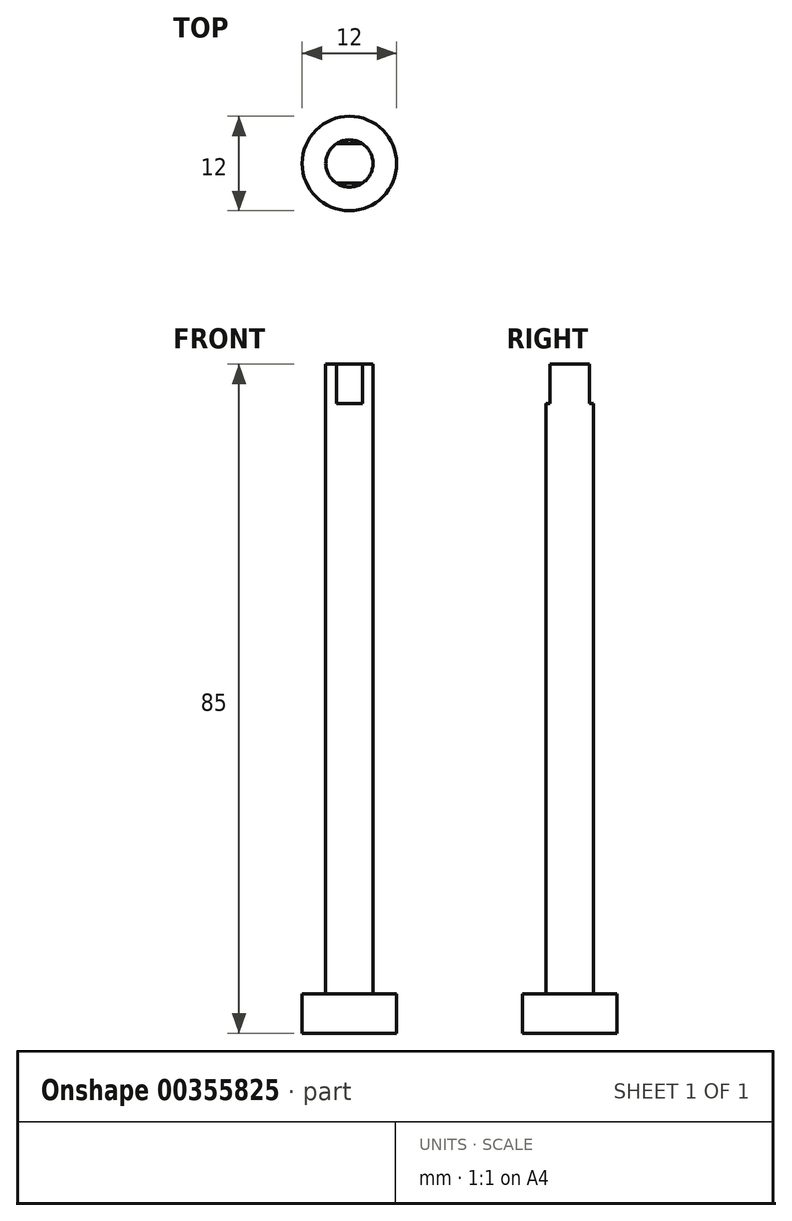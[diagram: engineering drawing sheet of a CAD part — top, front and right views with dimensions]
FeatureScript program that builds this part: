
annotation { "Feature Type Name" : "Feature", "Feature Type Description" : "" }
export const myFeature = defineFeature(function(context is Context, id is Id, definition is map)
    precondition{}
    {
        {
            var Q0;
            Q0=qCreatedBy(makeId("Top.planeOp"),FACE);
            var sketch = newSketch(context, id + "F0", { "sketchPlane" : qUnion([Q0])});
            skCircle(sketch, "E0", {"center": v(0, 0) * mm, "radius": 3 * mm});
            skSolve(sketch);
        }
        {
            var Q0;
            Q0 = qSketchRegion(id + "F0", true);
            extrude(context, id + "F1", {"entities" : qUnion([Q0]), "endBound" : BoundingType.SYMMETRIC, "depth" : 80 * mm});
        }
        {
            var Q0;
            Q0=makeQuery(id+"F1.opExtrude","CAP_FACE",FACE,{"disambiguationData":[OSD([sQuery(id+"F0.wireOp",EDGE,"E0")])],"isStart":true});
            var sketch = newSketch(context, id + "F2", { "sketchPlane" : qUnion([Q0])});
            skCircle(sketch, "E1", {"center": v(0, 0) * mm, "radius": 6 * mm});
            skSolve(sketch);
        }
        {
            var Q0;
            Q0=makeQuery(id+"F2.imprint","IMPRINT",FACE,{"disambiguationData":[TD([[makeQuery(id+"F2.imprint","IMPRINT",EDGE,{"derivedFrom":sQuery(id+"F2.wireOp",EDGE,"E1")}),1.0]])]});
            var Q1;
            Q1=makeQuery(id+"F2.imprint","IMPRINT",FACE,{"disambiguationData":[TD([[makeQuery(id+"F2.imprint","IMPRINT",EDGE,{"derivedFrom":makeQuery(id+"F1.opExtrude","CAP_EDGE",EDGE,{"disambiguationData":[OSD([sQuery(id+"F0.wireOp",EDGE,"E0")])],"isStart":true})}),-1.0]])]});
            extrude(context, id + "F3", {"entities" : qUnion([Q0, Q1]), "operationType" : NewBodyOperationType.ADD, "depth" : 5 * mm});
        }
        {
            var Q0;
            Q0=makeQuery(id+"F1.opExtrude","CAP_FACE",FACE,{"disambiguationData":[OSD([sQuery(id+"F0.wireOp",EDGE,"E0")])],"isStart":false});
            var sketch = newSketch(context, id + "F4", { "sketchPlane" : qUnion([Q0])});
            skLineSegment(sketch, "E2.bottom", {"start": v(4.53, -2.5) * mm, "end": v(-4.53, -2.5) * mm});
            skLineSegment(sketch, "E2.top", {"start": v(4.53, 2.5) * mm, "end": v(-4.53, 2.5) * mm});
            skLineSegment(sketch, "E2.left", {"start": v(4.53, -2.5) * mm, "end": v(4.53, 2.5) * mm});
            skLineSegment(sketch, "E2.right", {"start": v(-4.53, -2.5) * mm, "end": v(-4.53, 2.5) * mm});
            skPoint(sketch, "E2.middle", {"position": v(0, 0) * mm});
            skLineSegment(sketch, "E3.bottom", {"start": v(4.53, -3.8) * mm, "end": v(-4.53, -3.8) * mm});
            skLineSegment(sketch, "E3.top", {"start": v(4.53, 3.8) * mm, "end": v(-4.53, 3.8) * mm});
            skLineSegment(sketch, "E3.left", {"start": v(4.53, -3.8) * mm, "end": v(4.53, 3.8) * mm});
            skLineSegment(sketch, "E3.right", {"start": v(-4.53, -3.8) * mm, "end": v(-4.53, 3.8) * mm});
            skSolve(sketch);
        }
        {
            var Q0;
            {var subQ0=sQuery(id+"F4.wireOp",EDGE,"E3.top");Q0=makeQuery(id+"F4.imprint","IMPRINT",FACE,{"disambiguationData":[TD([[makeQuery(id+"F4.imprint","IMPRINT",EDGE,{"derivedFrom":subQ0}),1.0]])]});}
            var Q1;
            {var subQ0=sQuery(id+"F4.wireOp",EDGE,"E2.top");var subQ1=makeQuery(id+"F1.opExtrude","CAP_EDGE",EDGE,{"disambiguationData":[OSD([sQuery(id+"F0.wireOp",EDGE,"E0")])],"isStart":false});var subQ2=makeQuery(id+"F4.imprint","INTERSECT",VERTEX,{"disambiguationData":[OD(0.0)],"derivedFrom":[subQ1,subQ0]});Q1=makeQuery(id+"F4.imprint","IMPRINT",FACE,{"disambiguationData":[TD([[makeQuery(id+"F4.imprint","IMPRINT",EDGE,{"disambiguationData":[TD([[subQ2,-1.0]])],"derivedFrom":subQ0}),-1.0]])]});}
            var Q2;
            {var subQ0=sQuery(id+"F4.wireOp",EDGE,"E2.bottom");var subQ1=makeQuery(id+"F1.opExtrude","CAP_EDGE",EDGE,{"disambiguationData":[OSD([sQuery(id+"F0.wireOp",EDGE,"E0")])],"isStart":false});var subQ2=makeQuery(id+"F4.imprint","INTERSECT",VERTEX,{"disambiguationData":[OD(0.0)],"derivedFrom":[subQ1,subQ0]});Q2=makeQuery(id+"F4.imprint","IMPRINT",FACE,{"disambiguationData":[TD([[makeQuery(id+"F4.imprint","IMPRINT",EDGE,{"disambiguationData":[TD([[subQ2,-1.0]])],"derivedFrom":subQ0}),1.0]])]});}
            extrude(context, id + "F5", {"entities" : qUnion([Q0, Q1, Q2]), "operationType" : NewBodyOperationType.REMOVE, "oppositeDirection" : true, "depth" : 5 * mm});
        }
    });
